# Revit family: NAU_Naughtone_Stng_PullmanSofaWIP20
name_source: partatom
category: Furniture
revit_build: Autodesk Revit 2017 (Build: 20190508_0315(x64)
units: mm (PartAtom-declared; Revit-internal decimal feet)

## family parameters
Always vertical = Yes
Cut with Voids When Loaded = No
OmniClass Number = 23.40.20.00
OmniClass Title = General Furniture and Specialties
Room Calculation Point = No
Shared = Yes
Work Plane-Based = No

## types (4) — shared parameters
Assembly Code = E2020200
AssetType = Movable
BoothMaterial = NAU_Maharam_Fabric_Teatro_007Yellow
Category = Pr_40_50_12 : Chairs, seats and benches
Color = Various
CushionOffset = 700 mm  [stored 2.29659 ft]
DurationUnit = year
FrameMaterial = NAU_Naughtone_EPC_White
HasBackBoard = Yes
IfcExportAs = IfcFurnishingElementType
IfcExportType = SOFA
Keynote = Pr_40_50_12
LegMaterial = NAU_Naughtone_Metal_Steel_White
MainColor = Various
ManufacturerAddress = Knaresborough Tech Park, Manse Lane, Knaresborough, HG5 8LF
ManufacturerName = Naughtone
ManufacturerURL = www.naughtone.com
NBSDescription = Seating
NBSReference = 45-35-72/352
NominalHeight = 1300 mm  [stored 4.26509 ft]
NominalLength = 1900 mm  [stored 6.2336 ft]
NominalWidth = 626 mm  [stored 2.05381 ft]
ProductInformation = www.naughtone.com/products/pullman/
SeatMaterial = NAU_Maharam_Fabric_Teatro_007Yellow
Shape = Rectangular
Size = 1900 x 675 x 1300mm
SustainabilityPerformance = FSC certifeied, SCS indoor advantage gold
TableOffset = 421 mm  [stored 1.38123 ft]
TabletMaterial = NAU_Naughtone_Wood_Oak
URL = www.naughtone.com
Uniclass2015Code = Pr_40_50_12
Uniclass2015Title = Chairs, seats and benches
Uniclass2015Version = Products v1.15
Version = 1
WarrantyDescription = Request warranty information from naughtone
WarrantyDurationLabor = 7
WarrantyDurationParts = 7
WarrantyDurationUnit = year
zero-valued in all types: NumberOfChairs, WorksurfaceArea

## per-type parameters (varying)
| type | BIMObjectName | Description | Finish | IsLeftTablet | IsRightTablet | Material | Model | ModelNumber | ModelReference | Name |
| Pullman 3 seat sofa with 2 tablet arms PUL3HT2 | NAU_Naughtone_Seating_Pullman_Pullman3seatsofawith2tabletarms | Pullman 3 seat sofa with 2 tablet arms | Fabric upholstery; white EPC/black EPC/oak/walnut legs; whiteEPC/black EPC tablet arm; white MFMDF/black MFMDF/oak veneer MDF/walnut veneerMDF tablet top | Yes | Yes | Fabric, plywood frame, foam, steel or wood legs, steel tablet arm, wooden table top | PUL3HT2 | PUL3HT2 | Pullman 3 seat sofa with 2 tablet arms | Seating_Pullman_Pullman3seatsofawith2tabletarms_Naughtone |
| Pullman 3 seat sofa with tablet arm (left) PUL3HTL | NAU_Naughtone_Seating_Pullman_Pullman3seatsofawithtabletarmleft | Pullman 3 seat sofa with tablet arm left | Fabric upholstery; white EPC/black EPC/oak/walnut legs; whiteEPC/black EPC tablet arm; white MFMDF/black MFMDF/oak veneer MDF/walnut veneerMDF tablet top | Yes | No | Fabric, plywood frame, foam, steel or wood legs, steel tablet arm, wooden table top | PUL3HTL | PUL3HTL | Pullman 3 seat sofa with tablet arm left | Seating_Pullman_Pullman3seatsofawithtabletarmleft_Naughtone |
| Pullman 3 seat sofa with tablet arm (right) PUL3HTR | NAU_Naughtone_Seating_Pullman_Pullman3seatsofawithtabletarmright | Pullman 3 seat sofa with tablet arm right | Fabric upholstery; white EPC/black EPC/oak/walnut legs; whiteEPC/black EPC tablet arm; white MFMDF/black MFMDF/oak veneer MDF/walnut veneerMDF tablet top | No | Yes | Fabric, plywood frame, foam, steel or wood legs, steel tablet arm, wooden table top | PUL3HTR | PUL3HTR | Pullman 3 seat sofa with tablet arm right | Seating_Pullman_Pullman3seatsofawithtabletarmright_Naughtone |
| Pullman 3 seat sofa PUL3H | NAU_Naughtone_Seating_Pullman_Pullman3seatsofa | Pullman 3 seat sofa | Fabric upholstery; white EPC/black EPC/oak/walnut legs | No | No | Fabric, plywood frame, foam, steel or wood legs | PULB3H | PULB3H | Pullman 3 seat sofa | Seating_Pullman_Pullman3seatsofa_Naughtone
Seating_Pullman_Pullman3seatsofa_Naughtone |

note: [stored X ft] marks values corroborated as IEEE doubles in the binary element streams (Revit-internal decimal feet)

## geometry (parser evidence)
native form markers: Sweep x6
no freeform markers — native parametric forms only
